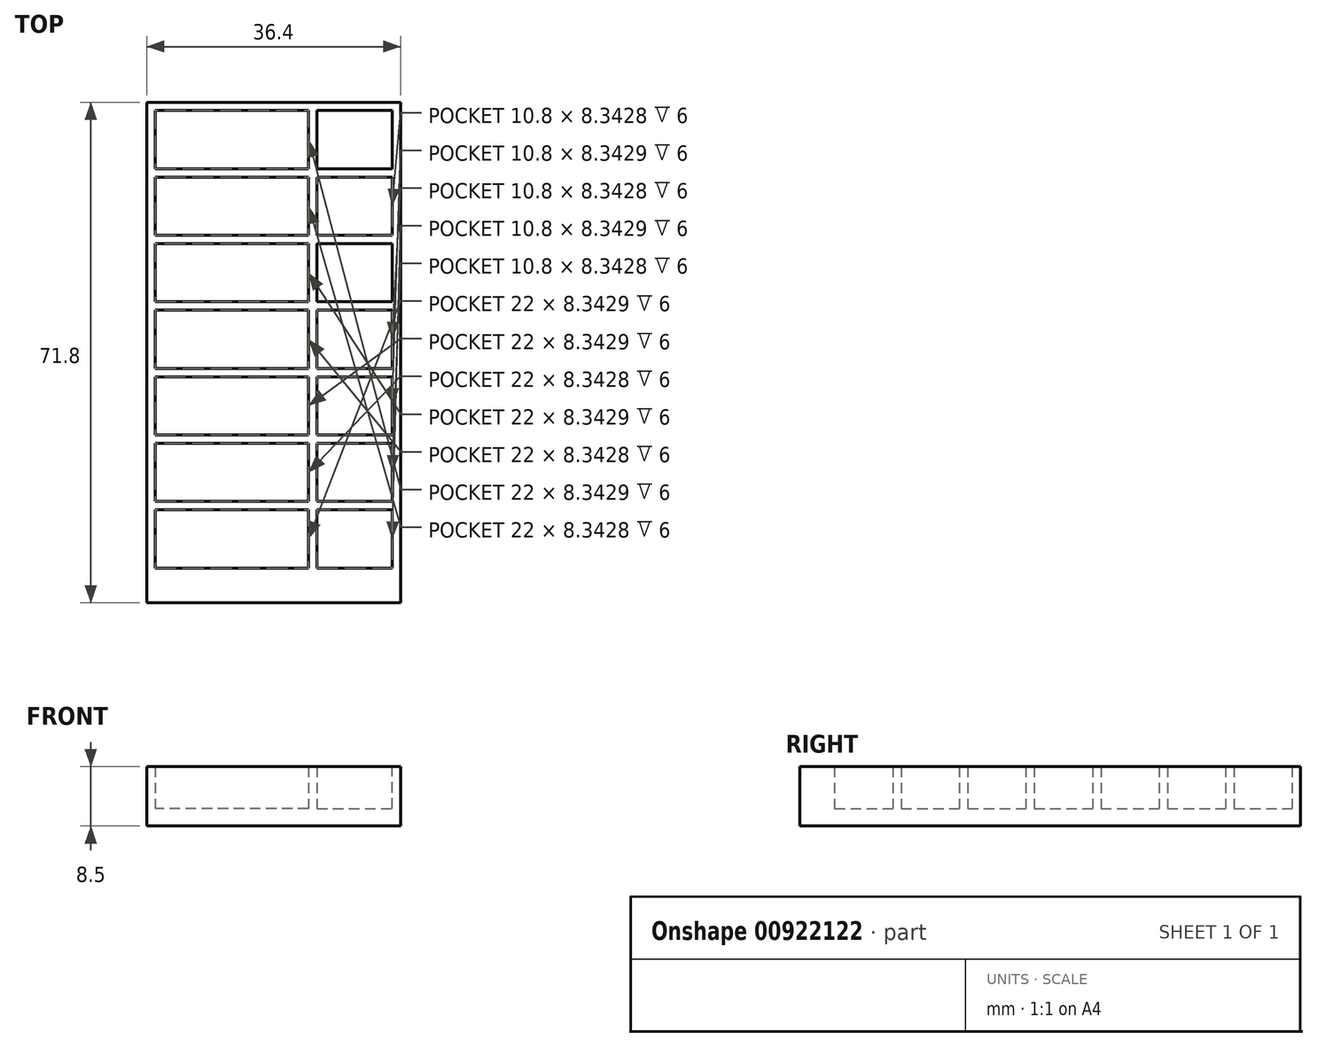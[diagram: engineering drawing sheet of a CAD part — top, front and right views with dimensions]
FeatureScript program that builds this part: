
annotation { "Feature Type Name" : "Feature", "Feature Type Description" : "" }
export const myFeature = defineFeature(function(context is Context, id is Id, definition is map)
    precondition{}
    {
        {
            var Q0;
            Q0=qCreatedBy(makeId("Top.planeOp"),FACE);
            var sketch = newSketch(context, id + "F0", { "sketchPlane" : qUnion([Q0])});
            skLineSegment(sketch, "E0.bottom", {"start": v(0, 0) * mm, "end": v(36.4, 0) * mm});
            skLineSegment(sketch, "E0.top", {"start": v(0, 71.8) * mm, "end": v(36.4, 71.8) * mm});
            skLineSegment(sketch, "E0.left", {"start": v(0, 0) * mm, "end": v(0, 71.8) * mm});
            skLineSegment(sketch, "E0.right", {"start": v(36.4, 0) * mm, "end": v(36.4, 71.8) * mm});
            skSolve(sketch);
        }
        {
            var Q0;
            Q0=qSketchRegion(id+"F0",true);
            extrude(context, id + "F1", {"entities" : qUnion([Q0]), "depth" : 8.5 * mm, "offsetDistance" : 25 * mm});
        }
        {
            var Q0;
            Q0=makeQuery(id+"F1.opExtrude","CAP_FACE",FACE,{"disambiguationData":[OSD([sQuery(id+"F0.wireOp",EDGE,"E0.bottom"),sQuery(id+"F0.wireOp",EDGE,"E0.top"),sQuery(id+"F0.wireOp",EDGE,"E0.left"),sQuery(id+"F0.wireOp",EDGE,"E0.right")])],"isStart":false});
            var sketch = newSketch(context, id + "F2", { "sketchPlane" : qUnion([Q0])});
            skLineSegment(sketch, "E1.0", {"start": v(1.2, 70.6) * mm, "end": v(35.2, 70.6) * mm});
            skLineSegment(sketch, "E2.0", {"start": v(35.2, 5) * mm, "end": v(35.2, 70.6) * mm});
            skLineSegment(sketch, "E3.0", {"start": v(1.2, 5) * mm, "end": v(1.2, 70.6) * mm});
            skLineSegment(sketch, "E4.0", {"start": v(1.2, 5) * mm, "end": v(35.2, 5) * mm});
            skSolve(sketch);
        }
        {
            var Q0;
            Q0=qSketchRegion(id+"F2",true);
            extrude(context, id + "F3", {"entities" : qUnion([Q0]), "operationType" : NewBodyOperationType.REMOVE, "oppositeDirection" : true, "depth" : 6 * mm, "offsetDistance" : 25 * mm});
        }
        {
            var Q0;
            Q0=makeQuery(id+"F3.boolean.opBoolean","COPY",FACE,{"derivedFrom":makeQuery(id+"F3.opExtrude","CAP_FACE",FACE,{"disambiguationData":[OSD([sQuery(id+"F2.wireOp",EDGE,"E1.0"),sQuery(id+"F2.wireOp",EDGE,"E2.0"),sQuery(id+"F2.wireOp",EDGE,"E3.0"),sQuery(id+"F2.wireOp",EDGE,"E4.0")])],"isStart":false})});
            var sketch = newSketch(context, id + "F4", { "sketchPlane" : qUnion([Q0])});
            skLineSegment(sketch, "E5.bottom", {"start": v(12, 70.6) * mm, "end": v(13.2, 70.6) * mm});
            skLineSegment(sketch, "E5.top", {"start": v(12, 5) * mm, "end": v(13.2, 5) * mm});
            skLineSegment(sketch, "E6.bottom", {"start": v(23.2, 70.6) * mm, "end": v(24.4, 70.6) * mm});
            skLineSegment(sketch, "E6.top", {"start": v(23.2, 5) * mm, "end": v(24.4, 5) * mm});
            skLineSegment(sketch, "E6.left", {"start": v(23.2, 70.6) * mm, "end": v(23.2, 62.26) * mm});
            skLineSegment(sketch, "E6.right", {"start": v(24.4, 70.6) * mm, "end": v(24.4, 62.26) * mm});
            skLineSegment(sketch, "E7", {"start": v(35.2, 70.6) * mm, "end": v(35.2, 5) * mm, "construction": true});
            skLineSegment(sketch, "E8", {"start": v(35.2, 5) * mm, "end": v(1.2, 5) * mm, "construction": true});
            skLineSegment(sketch, "E9.bottom", {"start": v(1.2, 62.26) * mm, "end": v(12, 62.26) * mm});
            skLineSegment(sketch, "E9.top", {"start": v(1.2, 61.06) * mm, "end": v(12, 61.06) * mm});
            skLineSegment(sketch, "E9.left", {"start": v(1.2, 62.26) * mm, "end": v(1.2, 61.06) * mm});
            skLineSegment(sketch, "E9.right", {"start": v(35.2, 62.26) * mm, "end": v(35.2, 61.06) * mm});
            skLineSegment(sketch, "E10.bottom", {"start": v(35.2, 52.71) * mm, "end": v(24.4, 52.71) * mm});
            skLineSegment(sketch, "E10.top", {"start": v(35.2, 51.51) * mm, "end": v(24.4, 51.51) * mm});
            skLineSegment(sketch, "E10.left", {"start": v(35.2, 52.71) * mm, "end": v(35.2, 51.51) * mm});
            skLineSegment(sketch, "E10.right", {"start": v(1.2, 52.71) * mm, "end": v(1.2, 51.51) * mm});
            skLineSegment(sketch, "E11.bottom", {"start": v(1.2, 43.17) * mm, "end": v(12, 43.17) * mm});
            skLineSegment(sketch, "E11.top", {"start": v(1.2, 41.97) * mm, "end": v(12, 41.97) * mm});
            skLineSegment(sketch, "E11.left", {"start": v(1.2, 43.17) * mm, "end": v(1.2, 41.97) * mm});
            skLineSegment(sketch, "E11.right", {"start": v(35.2, 43.17) * mm, "end": v(35.2, 41.97) * mm});
            skLineSegment(sketch, "E12.bottom", {"start": v(35.2, 33.63) * mm, "end": v(24.4, 33.63) * mm});
            skLineSegment(sketch, "E12.top", {"start": v(35.2, 32.43) * mm, "end": v(24.4, 32.43) * mm});
            skLineSegment(sketch, "E12.left", {"start": v(35.2, 33.63) * mm, "end": v(35.2, 32.43) * mm});
            skLineSegment(sketch, "E12.right", {"start": v(1.2, 33.63) * mm, "end": v(1.2, 32.43) * mm});
            skLineSegment(sketch, "E13.bottom", {"start": v(1.2, 24.09) * mm, "end": v(12, 24.09) * mm});
            skLineSegment(sketch, "E13.top", {"start": v(1.2, 22.89) * mm, "end": v(12, 22.89) * mm});
            skLineSegment(sketch, "E13.left", {"start": v(1.2, 24.09) * mm, "end": v(1.2, 22.89) * mm});
            skLineSegment(sketch, "E13.right", {"start": v(35.2, 24.09) * mm, "end": v(35.2, 22.89) * mm});
            skLineSegment(sketch, "E14.bottom", {"start": v(35.2, 14.54) * mm, "end": v(24.4, 14.54) * mm});
            skLineSegment(sketch, "E14.top", {"start": v(35.2, 13.34) * mm, "end": v(24.4, 13.34) * mm});
            skLineSegment(sketch, "E14.left", {"start": v(35.2, 14.54) * mm, "end": v(35.2, 13.34) * mm});
            skLineSegment(sketch, "E14.right", {"start": v(1.2, 14.54) * mm, "end": v(1.2, 13.34) * mm});
            skLineSegment(sketch, "E15.trimOffspring", {"start": v(13.2, 62.26) * mm, "end": v(23.2, 62.26) * mm});
            skLineSegment(sketch, "E16.trimOffspring", {"start": v(13.2, 61.06) * mm, "end": v(23.2, 61.06) * mm});
            skLineSegment(sketch, "E17.trimOffspring", {"start": v(23.2, 61.06) * mm, "end": v(23.2, 52.71) * mm});
            skLineSegment(sketch, "E18.trimOffspring", {"start": v(24.4, 62.26) * mm, "end": v(35.2, 62.26) * mm});
            skLineSegment(sketch, "E19.trimOffspring", {"start": v(24.4, 61.06) * mm, "end": v(24.4, 52.71) * mm});
            skLineSegment(sketch, "E20.trimOffspring", {"start": v(24.4, 61.06) * mm, "end": v(35.2, 61.06) * mm});
            skLineSegment(sketch, "E21.trimOffspring", {"start": v(23.2, 52.71) * mm, "end": v(13.2, 52.71) * mm});
            skLineSegment(sketch, "E22.trimOffspring", {"start": v(23.2, 51.51) * mm, "end": v(13.2, 51.51) * mm});
            skLineSegment(sketch, "E23.trimOffspring", {"start": v(23.2, 51.51) * mm, "end": v(23.2, 43.17) * mm});
            skLineSegment(sketch, "E24.trimOffspring", {"start": v(24.4, 51.51) * mm, "end": v(24.4, 43.17) * mm});
            skLineSegment(sketch, "E25.trimOffspring", {"start": v(12, 52.71) * mm, "end": v(1.2, 52.71) * mm});
            skLineSegment(sketch, "E26.trimOffspring", {"start": v(12, 51.51) * mm, "end": v(1.2, 51.51) * mm});
            skLineSegment(sketch, "E27.trimOffspring", {"start": v(13.2, 43.17) * mm, "end": v(23.2, 43.17) * mm});
            skLineSegment(sketch, "E28.trimOffspring", {"start": v(13.2, 41.97) * mm, "end": v(23.2, 41.97) * mm});
            skLineSegment(sketch, "E29.trimOffspring", {"start": v(23.2, 41.97) * mm, "end": v(23.2, 33.63) * mm});
            skLineSegment(sketch, "E30.trimOffspring", {"start": v(24.4, 43.17) * mm, "end": v(35.2, 43.17) * mm});
            skLineSegment(sketch, "E31.trimOffspring", {"start": v(24.4, 41.97) * mm, "end": v(24.4, 33.63) * mm});
            skLineSegment(sketch, "E32.trimOffspring", {"start": v(24.4, 41.97) * mm, "end": v(35.2, 41.97) * mm});
            skLineSegment(sketch, "E33.trimOffspring", {"start": v(23.2, 33.63) * mm, "end": v(13.2, 33.63) * mm});
            skLineSegment(sketch, "E34.trimOffspring", {"start": v(23.2, 32.43) * mm, "end": v(13.2, 32.43) * mm});
            skLineSegment(sketch, "E35.trimOffspring", {"start": v(24.4, 32.43) * mm, "end": v(24.4, 24.09) * mm});
            skLineSegment(sketch, "E36.trimOffspring", {"start": v(23.2, 32.43) * mm, "end": v(23.2, 24.09) * mm});
            skLineSegment(sketch, "E37.trimOffspring", {"start": v(12, 33.63) * mm, "end": v(1.2, 33.63) * mm});
            skLineSegment(sketch, "E38.trimOffspring", {"start": v(12, 32.43) * mm, "end": v(1.2, 32.43) * mm});
            skLineSegment(sketch, "E39.trimOffspring", {"start": v(13.2, 24.09) * mm, "end": v(23.2, 24.09) * mm});
            skLineSegment(sketch, "E40.trimOffspring", {"start": v(13.2, 22.89) * mm, "end": v(23.2, 22.89) * mm});
            skLineSegment(sketch, "E41.trimOffspring", {"start": v(23.2, 22.89) * mm, "end": v(23.2, 14.54) * mm});
            skLineSegment(sketch, "E42.trimOffspring", {"start": v(24.4, 24.09) * mm, "end": v(35.2, 24.09) * mm});
            skLineSegment(sketch, "E43.trimOffspring", {"start": v(24.4, 22.89) * mm, "end": v(24.4, 14.54) * mm});
            skLineSegment(sketch, "E44.trimOffspring", {"start": v(24.4, 22.89) * mm, "end": v(35.2, 22.89) * mm});
            skLineSegment(sketch, "E45.trimOffspring", {"start": v(23.2, 14.54) * mm, "end": v(13.2, 14.54) * mm});
            skLineSegment(sketch, "E46.trimOffspring", {"start": v(24.4, 13.34) * mm, "end": v(24.4, 5) * mm});
            skLineSegment(sketch, "E47.trimOffspring", {"start": v(23.2, 13.34) * mm, "end": v(13.2, 13.34) * mm});
            skLineSegment(sketch, "E48.trimOffspring", {"start": v(23.2, 13.34) * mm, "end": v(23.2, 5) * mm});
            skLineSegment(sketch, "E49.trimOffspring", {"start": v(12, 14.54) * mm, "end": v(1.2, 14.54) * mm});
            skLineSegment(sketch, "E50.trimOffspring", {"start": v(12, 13.34) * mm, "end": v(1.2, 13.34) * mm});
            skLineSegment(sketch, "E51", {"start": v(12, 62.26) * mm, "end": v(13.2, 62.26) * mm});
            skLineSegment(sketch, "E52", {"start": v(13.2, 61.06) * mm, "end": v(12, 61.06) * mm});
            skLineSegment(sketch, "E53", {"start": v(12, 52.71) * mm, "end": v(13.2, 52.71) * mm});
            skLineSegment(sketch, "E54", {"start": v(13.2, 51.51) * mm, "end": v(12, 51.51) * mm});
            skLineSegment(sketch, "E55", {"start": v(12, 43.17) * mm, "end": v(13.2, 43.17) * mm});
            skLineSegment(sketch, "E56", {"start": v(13.2, 41.97) * mm, "end": v(12, 41.97) * mm});
            skLineSegment(sketch, "E57", {"start": v(12, 33.63) * mm, "end": v(13.2, 33.63) * mm});
            skLineSegment(sketch, "E58", {"start": v(13.2, 32.43) * mm, "end": v(12, 32.43) * mm});
            skLineSegment(sketch, "E59", {"start": v(12, 24.09) * mm, "end": v(13.2, 24.09) * mm});
            skLineSegment(sketch, "E60", {"start": v(13.2, 22.89) * mm, "end": v(12, 22.89) * mm});
            skLineSegment(sketch, "E61", {"start": v(12, 14.54) * mm, "end": v(13.2, 14.54) * mm});
            skLineSegment(sketch, "E62", {"start": v(13.2, 13.34) * mm, "end": v(12, 13.34) * mm});
            skSolve(sketch);
        }
        {
            var Q0;
            Q0=qSketchRegion(id+"F4",true);
            extrude(context, id + "F5", {"entities" : qUnion([Q0]), "operationType" : NewBodyOperationType.ADD, "depth" : 6 * mm, "offsetDistance" : 25 * mm});
        }
        {
            var Q0;
            Q0=makeQuery(id+"F1.opExtrude","SWEPT_BODY",BODY,{"disambiguationData":[OSD([sQuery(id+"F0.wireOp",EDGE,"E0.bottom"),sQuery(id+"F0.wireOp",EDGE,"E0.top"),sQuery(id+"F0.wireOp",EDGE,"E0.left"),sQuery(id+"F0.wireOp",EDGE,"E0.right")])]});
            transform(context, id + "F6", {"entities" : qUnion([Q0]), "transformType" : TransformType.TRANSLATION_3D, "dx" : 0 * mm, "dy" : 0 * mm, "dz" : 0 * mm, "makeCopy" : true});
        }
        {
            var Q0;
            Q0=makeQuery(id+"F6.opPattern","COPY",BODY,{"derivedFrom":makeQuery(id+"F1.opExtrude","SWEPT_BODY",BODY,{"disambiguationData":[OSD([sQuery(id+"F0.wireOp",EDGE,"E0.bottom"),sQuery(id+"F0.wireOp",EDGE,"E0.top"),sQuery(id+"F0.wireOp",EDGE,"E0.left"),sQuery(id+"F0.wireOp",EDGE,"E0.right")])]}),"instanceName":"1"});
            deleteBodies(context, id + "F7", {"entities" : qUnion([Q0])});
        }
    });
